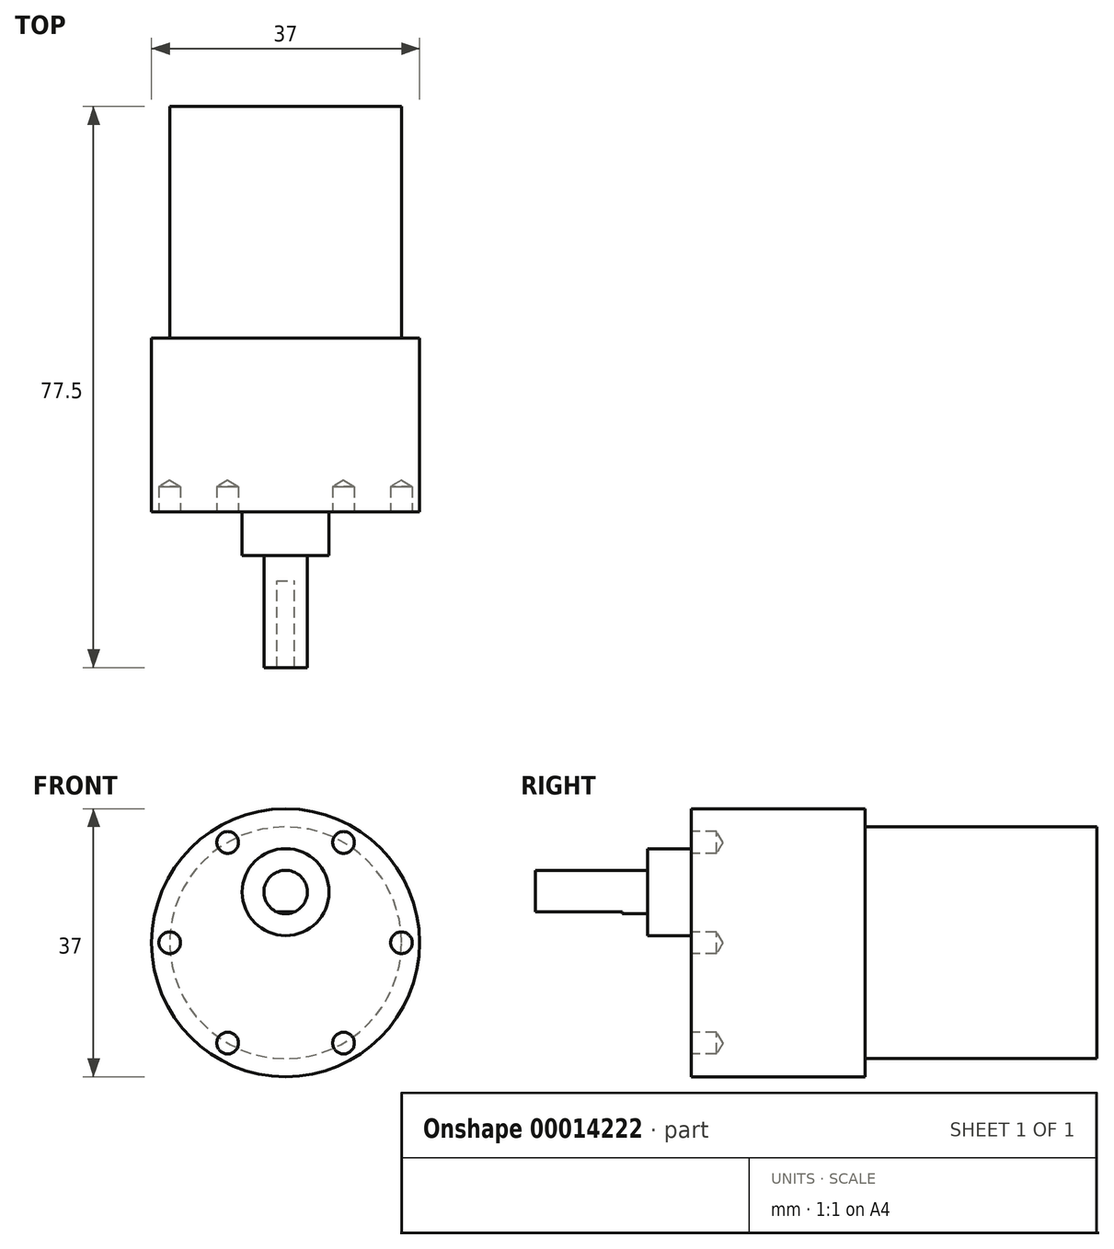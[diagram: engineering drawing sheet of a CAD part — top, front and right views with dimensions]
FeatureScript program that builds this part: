
annotation { "Feature Type Name" : "Feature", "Feature Type Description" : "" }
export const myFeature = defineFeature(function(context is Context, id is Id, definition is map)
    precondition{}
    {
        {
            var Q0;
            Q0=qCreatedBy(makeId("Right.planeOp"),FACE);
            var sketch = newSketch(context, id + "F0", { "sketchPlane" : qUnion([Q0])});
            skLineSegment(sketch, "E0", {"start": v(0, 0) * mm, "end": v(-24, 0) * mm});
            skLineSegment(sketch, "E1", {"start": v(0, 0) * mm, "end": v(0, 18.5) * mm});
            skLineSegment(sketch, "E2", {"start": v(-24, 0) * mm, "end": v(-24, 18.5) * mm});
            skLineSegment(sketch, "E3", {"start": v(-24, 18.5) * mm, "end": v(0, 18.5) * mm});
            skLineSegment(sketch, "E4", {"start": v(0, 0) * mm, "end": v(-75.03, 0) * mm, "construction": true});
            skLineSegment(sketch, "E5.MirrorCS", {"start": v(0, 0) * mm, "end": v(75.03, 0) * mm, "construction": true});
            skLineSegment(sketch, "E6", {"start": v(0, 0) * mm, "end": v(32, 0) * mm});
            skLineSegment(sketch, "E7", {"start": v(32, 0) * mm, "end": v(32, 16) * mm});
            skLineSegment(sketch, "E8", {"start": v(32, 16) * mm, "end": v(0, 16) * mm});
            skSolve(sketch);
        }
        {
            var Q0;
            {var subQ3=sQuery(id+"F0.wireOp",EDGE,"E0");Q0=makeQuery(id+"F0.imprint","IMPRINT",FACE,{"disambiguationData":[TD([[makeQuery(id+"F0.imprint","IMPRINT",EDGE,{"derivedFrom":subQ3}),-1.0]])]});}
            var Q1;
            {var subQ0=sQuery(id+"F0.wireOp",EDGE,"E6");Q1=makeQuery(id+"F0.imprint","IMPRINT",FACE,{"disambiguationData":[TD([[makeQuery(id+"F0.imprint","IMPRINT",EDGE,{"derivedFrom":subQ0}),1.0]])]});}
            var Q2;
            Q2=sQuery(id+"F0.wireOp",EDGE,"E4");
            revolve(context, id + "F1", {"entities" : qUnion([Q0, Q1]), "axis" : qUnion([Q2]), "revolveType" : RevolveType.FULL});
        }
        {
            var Q0;
            Q0=makeQuery(id+"F1.opRevolve","SWEPT_FACE",FACE,{"disambiguationData":[OSD([sQuery(id+"F0.wireOp",EDGE,"E2")])]});
            var sketch = newSketch(context, id + "F2", { "sketchPlane" : qUnion([Q0])});
            skCircle(sketch, "E9", {"center": v(0, 0) * mm, "radius": 16 * mm, "construction": true});
            skLineSegment(sketch, "E10", {"start": v(0, 0) * mm, "end": v(-16, 0) * mm, "construction": true});
            skLineSegment(sketch, "E11", {"start": v(0, 0) * mm, "end": v(16, 0) * mm, "construction": true});
            skLineSegment(sketch, "E12", {"start": v(0, 0) * mm, "end": v(-8, 13.86) * mm, "construction": true});
            skLineSegment(sketch, "E13.MirrorCS", {"start": v(0, 0) * mm, "end": v(8, 13.86) * mm, "construction": true});
            skLineSegment(sketch, "E14.MirrorCS", {"start": v(0, 0) * mm, "end": v(8, -13.86) * mm, "construction": true});
            skLineSegment(sketch, "E15.MirrorCS", {"start": v(0, 0) * mm, "end": v(-8, -13.86) * mm, "construction": true});
            skCircle(sketch, "E16", {"center": v(-8, 13.86) * mm, "radius": 1.5 * mm});
            skCircle(sketch, "E17.MirrorC", {"center": v(8, 13.86) * mm, "radius": 1.5 * mm});
            skCircle(sketch, "E18.MirrorC", {"center": v(-8, -13.86) * mm, "radius": 1.5 * mm});
            skCircle(sketch, "E19.MirrorC", {"center": v(8, -13.86) * mm, "radius": 1.5 * mm});
            skCircle(sketch, "E20", {"center": v(-16, 0) * mm, "radius": 1.5 * mm});
            skCircle(sketch, "E21.MirrorC", {"center": v(16, 0) * mm, "radius": 1.5 * mm});
            skLineSegment(sketch, "E22", {"start": v(0, 0) * mm, "end": v(0, 7) * mm, "construction": true});
            skCircle(sketch, "E23", {"center": v(0, 7) * mm, "radius": 6 * mm});
            skCircle(sketch, "E24", {"center": v(0, 7) * mm, "radius": 3 * mm});
            skCircle(sketch, "E25", {"center": v(0, 7) * mm, "radius": 2.75 * mm, "construction": true});
            skLineSegment(sketch, "E26", {"start": v(0, 7) * mm, "end": v(0, 4.25) * mm, "construction": true});
            skLineSegment(sketch, "E27", {"start": v(0, 4.25) * mm, "end": v(-1.2, 4.25) * mm});
            skLineSegment(sketch, "E28.MirrorCS", {"start": v(0, 4.25) * mm, "end": v(1.2, 4.25) * mm});
            skSolve(sketch);
        }
        {
            var Q0;
            Q0=sQuery(id+"F2.wireOp",VERTEX,"E10.end");
            var Q1;
            Q1=sQuery(id+"F2.wireOp",VERTEX,"E18.MirrorC.center");
            var Q2;
            Q2=sQuery(id+"F2.wireOp",VERTEX,"E19.MirrorC.center");
            var Q3;
            Q3=sQuery(id+"F2.wireOp",VERTEX,"E11.end");
            var Q4;
            Q4=sQuery(id+"F2.wireOp",VERTEX,"E17.MirrorC.center");
            var Q5;
            Q5=sQuery(id+"F2.wireOp",VERTEX,"E12.end");
            var Q6;
            Q6=makeQuery(id+"F1.opRevolve","SWEPT_BODY",BODY,{"disambiguationData":[OSD([sQuery(id+"F0.wireOp",EDGE,"E0"),sQuery(id+"F0.wireOp",EDGE,"E1"),sQuery(id+"F0.wireOp",EDGE,"E2"),sQuery(id+"F0.wireOp",EDGE,"E3"),sQuery(id+"F0.wireOp",EDGE,"E6"),sQuery(id+"F0.wireOp",EDGE,"E7"),sQuery(id+"F0.wireOp",EDGE,"E8")])]});
            hole(context, id + "F3", {"style" : HoleStyle.SIMPLE, "holeDiameter" : 3 * mm, "endStyle" : HoleEndStyle.BLIND, "holeDepth" : 3.5 * mm, "locations" : qUnion([Q0, Q1, Q2, Q3, Q4, Q5]), "scope" : qUnion([Q6])});
        }
        {
            var Q0;
            Q0=makeQuery(id+"F2.imprint","IMPRINT",FACE,{"disambiguationData":[TD([[makeQuery(id+"F2.imprint","IMPRINT",EDGE,{"derivedFrom":sQuery(id+"F2.wireOp",EDGE,"E23")}),1.0]])]});
            extrude(context, id + "F4", {"entities" : qUnion([Q0]), "operationType" : NewBodyOperationType.ADD, "depth" : 6 * mm});
        }
        {
            var Q0;
            {var subQ0=sQuery(id+"F2.wireOp",EDGE,"E27");Q0=makeQuery(id+"F2.imprint","IMPRINT",FACE,{"disambiguationData":[TD([[makeQuery(id+"F2.imprint","IMPRINT",EDGE,{"derivedFrom":subQ0}),-1.0]])]});}
            extrude(context, id + "F5", {"entities" : qUnion([Q0]), "operationType" : NewBodyOperationType.ADD, "depth" : 21.5 * mm});
        }
        {
            var Q0;
            {var subQ0=sQuery(id+"F2.wireOp",EDGE,"E27");Q0=makeQuery(id+"F2.imprint","IMPRINT",FACE,{"disambiguationData":[TD([[makeQuery(id+"F2.imprint","IMPRINT",EDGE,{"derivedFrom":subQ0}),1.0]])]});}
            extrude(context, id + "F6", {"entities" : qUnion([Q0]), "operationType" : NewBodyOperationType.ADD, "depth" : 9.5 * mm});
        }
    });
